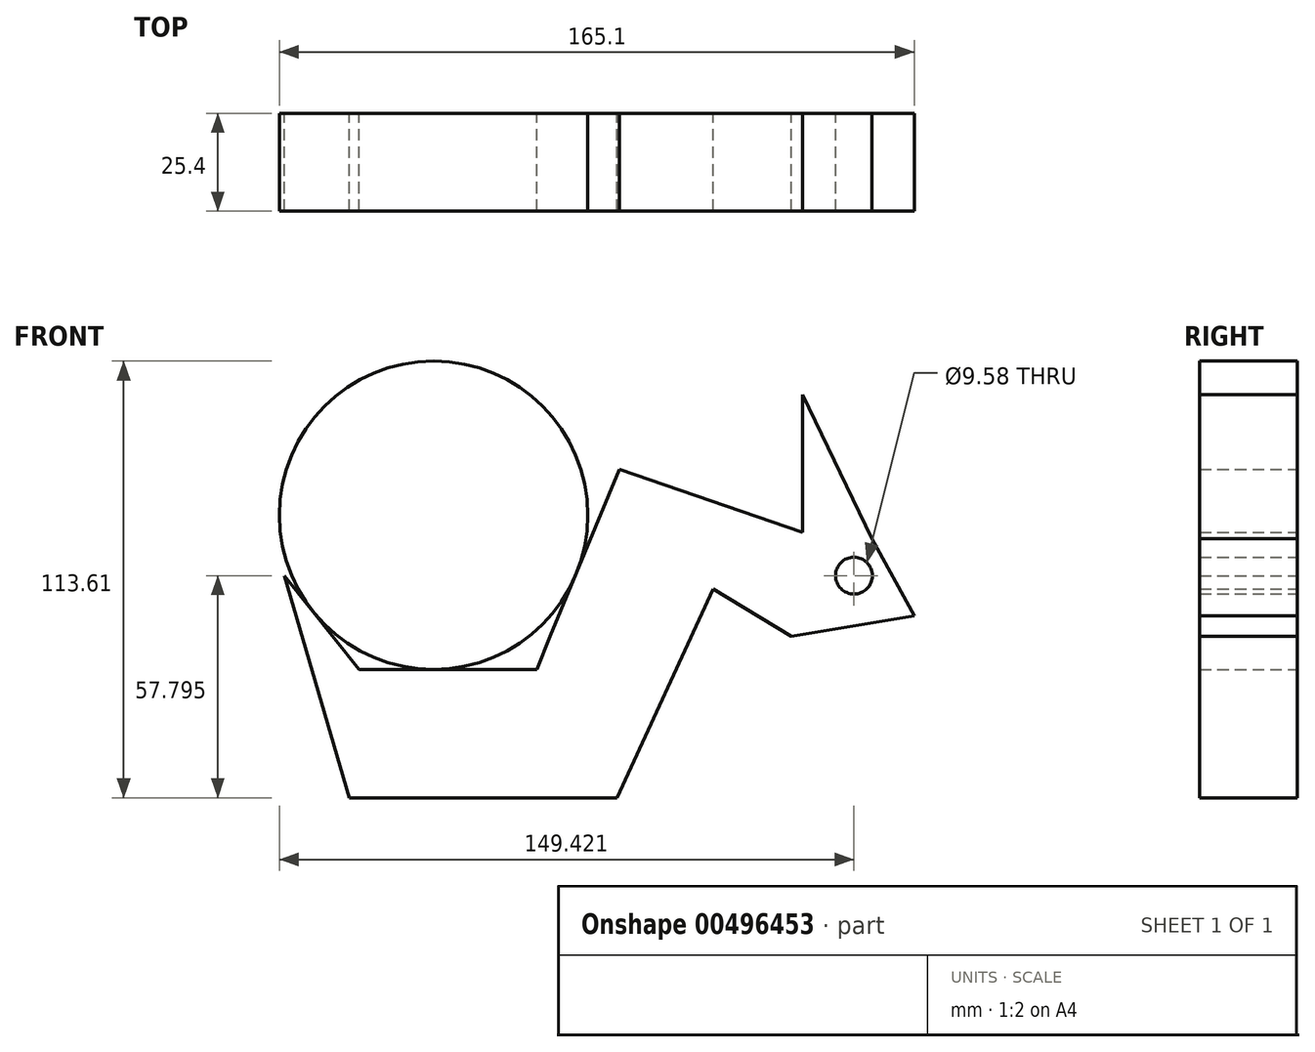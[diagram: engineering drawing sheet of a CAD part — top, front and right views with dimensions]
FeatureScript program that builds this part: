
annotation { "Feature Type Name" : "Feature", "Feature Type Description" : "" }
export const myFeature = defineFeature(function(context is Context, id is Id, definition is map)
    precondition{}
    {
        {
            var Q0;
            Q0=qCreatedBy(makeId("Front.planeOp"),FACE);
            var sketch = newSketch(context, id + "F0", { "sketchPlane" : qUnion([Q0])});
            skLineSegment(sketch, "E0", {"start": v(63.57, 12.34) * mm, "end": v(38.6, -41.96) * mm});
            skLineSegment(sketch, "E1", {"start": v(38.6, -41.96) * mm, "end": v(-31, -41.96) * mm});
            skLineSegment(sketch, "E2", {"start": v(-31, -41.96) * mm, "end": v(-47.84, 15.83) * mm});
            skLineSegment(sketch, "E3", {"start": v(-47.84, 15.83) * mm, "end": v(-28.39, -8.56) * mm});
            skLineSegment(sketch, "E4", {"start": v(-28.39, -8.56) * mm, "end": v(17.72, -8.56) * mm});
            skLineSegment(sketch, "E5", {"start": v(21.26, 0) * mm, "end": v(17.72, -8.56) * mm});
            skLineSegment(sketch, "E6", {"start": v(21.26, 0) * mm, "end": v(39.27, 43.42) * mm});
            skLineSegment(sketch, "E7", {"start": v(39.27, 43.42) * mm, "end": v(86.88, 27.16) * mm});
            skLineSegment(sketch, "E8", {"start": v(86.88, 27.16) * mm, "end": v(86.88, 62.87) * mm});
            skLineSegment(sketch, "E9", {"start": v(86.88, 62.87) * mm, "end": v(104.89, 25.42) * mm});
            skLineSegment(sketch, "E10", {"start": v(104.89, 25.42) * mm, "end": v(115.92, 5.38) * mm});
            skLineSegment(sketch, "E11", {"start": v(115.92, 5.38) * mm, "end": v(83.98, 0) * mm});
            skLineSegment(sketch, "E12", {"start": v(83.98, 0) * mm, "end": v(63.57, 12.34) * mm});
            skCircle(sketch, "E13", {"center": v(100.24, 15.83) * mm, "radius": 4.79 * mm});
            skPoint(sketch, "E14.0.internal.snap0", {"position": v(95.89, 44.14) * mm});
            skFitSpline(sketch, "E14", {"points": [v(95.89, 2) * mm, v(90.37, 3.64) * mm, v(86.88, 9.74) * mm], "startDerivative": vector(-12.8, 1.5) * mm, "endDerivative": vector(-5.33, 13.76) * mm});
            skSolve(sketch);
        }
        {
            var Q0;
            Q0=qCreatedBy(makeId("Front.planeOp"),FACE);
            var sketch = newSketch(context, id + "F1", { "sketchPlane" : qUnion([Q0])});
            skCircle(sketch, "E15", {"center": v(-9.07, 31.54) * mm, "radius": 40.1 * mm});
            skSolve(sketch);
        }
        {
            var Q0;
            Q0=makeQuery(id+"F0.imprint","IMPRINT",FACE,{"disambiguationData":[TD([[makeQuery(id+"F0.imprint","IMPRINT",EDGE,{"derivedFrom":sQuery(id+"F0.wireOp",EDGE,"E0")}),-1.0]])]});
            var Q1;
            Q1=makeQuery(id+"F1.imprint","IMPRINT",FACE,{"disambiguationData":[TD([[makeQuery(id+"F1.imprint","IMPRINT",EDGE,{"derivedFrom":sQuery(id+"F1.wireOp",EDGE,"E15")}),1.0]])]});
            extrude(context, id + "F2", {"entities" : qUnion([Q0, Q1]), "depth" : 25.4 * mm});
        }
    });
